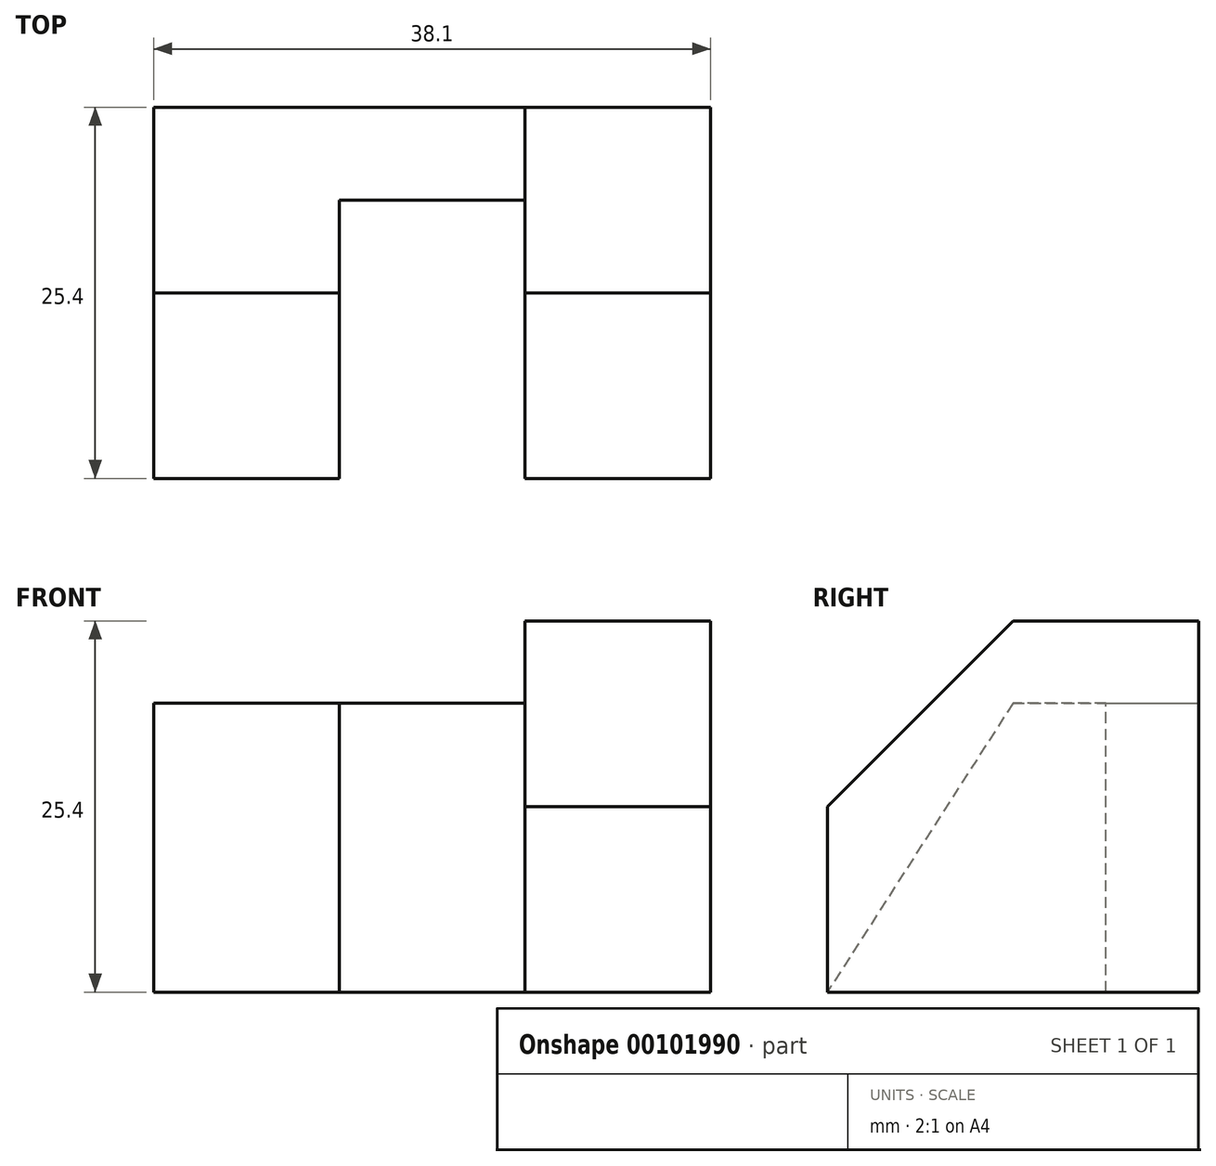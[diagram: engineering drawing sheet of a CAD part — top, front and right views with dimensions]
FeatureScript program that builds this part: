
annotation { "Feature Type Name" : "Feature", "Feature Type Description" : "" }
export const myFeature = defineFeature(function(context is Context, id is Id, definition is map)
    precondition{}
    {
        {
            var Q0;
            Q0=qCreatedBy(makeId("Right.planeOp"),FACE);
            var sketch = newSketch(context, id + "F0", { "sketchPlane" : qUnion([Q0])});
            skLineSegment(sketch, "E0", {"start": v(-18.67, -12.6) * mm, "end": v(6.73, -12.6) * mm});
            skLineSegment(sketch, "E1", {"start": v(6.73, -12.6) * mm, "end": v(6.73, 12.8) * mm});
            skLineSegment(sketch, "E2", {"start": v(6.73, 12.8) * mm, "end": v(-5.97, 12.8) * mm});
            skLineSegment(sketch, "E3", {"start": v(-5.97, 12.8) * mm, "end": v(-18.67, 0.1) * mm});
            skLineSegment(sketch, "E4", {"start": v(-18.67, 0.1) * mm, "end": v(-18.67, -12.6) * mm});
            skLineSegment(sketch, "E5", {"start": v(0.38, -12.6) * mm, "end": v(0.38, 7.18) * mm});
            skLineSegment(sketch, "E6", {"start": v(0.38, 7.18) * mm, "end": v(6.73, 7.18) * mm});
            skLineSegment(sketch, "E7", {"start": v(6.73, 7.18) * mm, "end": v(-5.97, 7.18) * mm});
            skLineSegment(sketch, "E8", {"start": v(-5.97, 7.18) * mm, "end": v(-18.67, -12.6) * mm});
            skSolve(sketch);
        }
        {
            var Q0;
            {var subQ3=sQuery(id+"F0.wireOp",EDGE,"E5");Q0=makeQuery(id+"F0.imprint","IMPRINT",FACE,{"disambiguationData":[TD([[makeQuery(id+"F0.imprint","IMPRINT",EDGE,{"derivedFrom":subQ3}),-1.0]])]});}
            extrude(context, id + "F1", {"entities" : qUnion([Q0]), "oppositeDirection" : true, "depth" : 25.4 * mm});
        }
        {
            var Q0;
            {var subQ2=sQuery(id+"F0.wireOp",EDGE,"E5");Q0=makeQuery(id+"F0.imprint","IMPRINT",FACE,{"disambiguationData":[TD([[makeQuery(id+"F0.imprint","IMPRINT",EDGE,{"derivedFrom":subQ2}),1.0]])]});}
            extrude(context, id + "F2", {"entities" : qUnion([Q0]), "operationType" : NewBodyOperationType.ADD, "oppositeDirection" : true, "depth" : 25.4 * mm, "hasSecondDirection" : true, "secondDirectionOppositeDirection" : true, "secondDirectionDepth" : 12.7 * mm});
        }
        {
            var Q0;
            {var subQ0=sQuery(id+"F0.wireOp",EDGE,"E2");Q0=makeQuery(id+"F0.imprint","IMPRINT",FACE,{"disambiguationData":[TD([[makeQuery(id+"F0.imprint","IMPRINT",EDGE,{"derivedFrom":subQ0}),1.0]])]});}
            var Q1;
            {var subQ3=sQuery(id+"F0.wireOp",EDGE,"E5");Q1=makeQuery(id+"F0.imprint","IMPRINT",FACE,{"disambiguationData":[TD([[makeQuery(id+"F0.imprint","IMPRINT",EDGE,{"derivedFrom":subQ3}),-1.0]])]});}
            var Q2;
            {var subQ2=sQuery(id+"F0.wireOp",EDGE,"E5");Q2=makeQuery(id+"F0.imprint","IMPRINT",FACE,{"disambiguationData":[TD([[makeQuery(id+"F0.imprint","IMPRINT",EDGE,{"derivedFrom":subQ2}),1.0]])]});}
            extrude(context, id + "F3", {"entities" : qUnion([Q0, Q1, Q2]), "operationType" : NewBodyOperationType.ADD, "depth" : 12.7 * mm});
        }
    });
